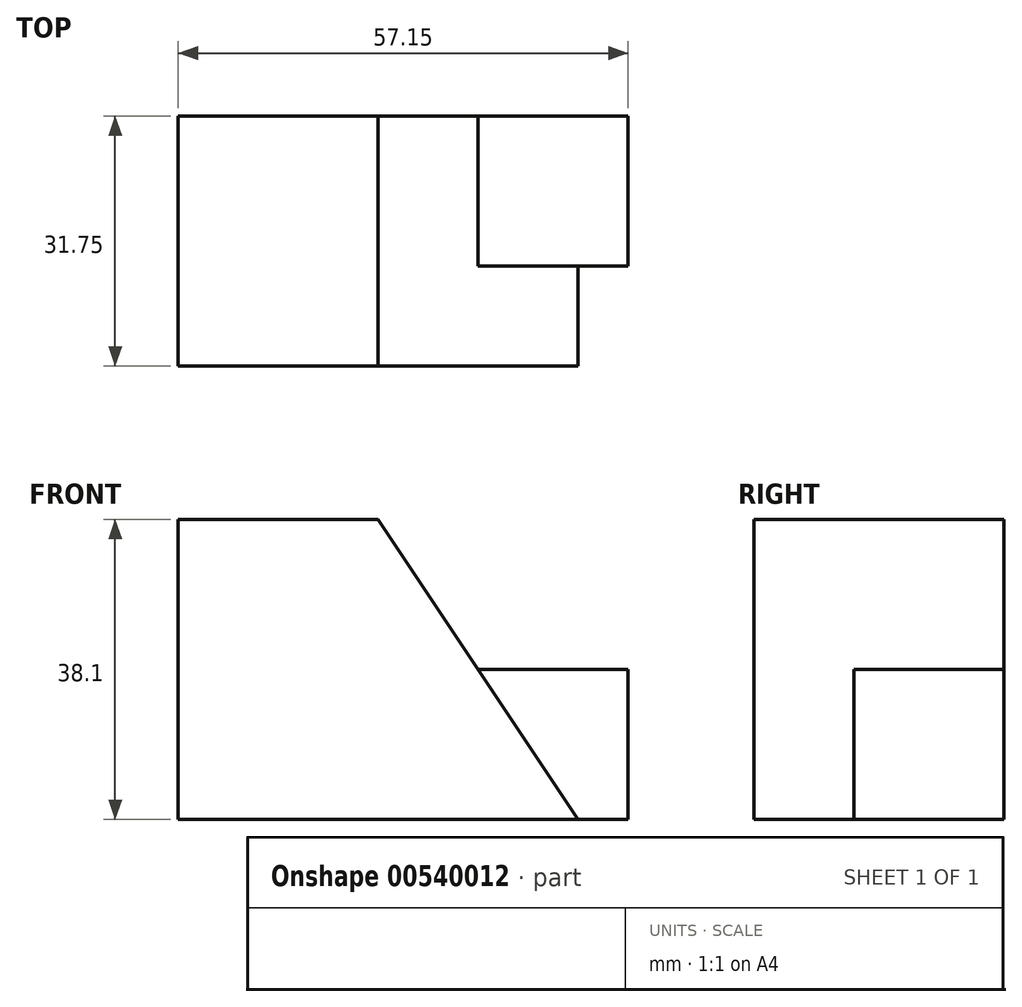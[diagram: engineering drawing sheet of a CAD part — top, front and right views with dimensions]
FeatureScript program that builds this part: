
annotation { "Feature Type Name" : "Feature", "Feature Type Description" : "" }
export const myFeature = defineFeature(function(context is Context, id is Id, definition is map)
    precondition{}
    {
        {
            var Q0;
            Q0=qCreatedBy(makeId("Front.planeOp"),FACE);
            var sketch = newSketch(context, id + "F0", { "sketchPlane" : qUnion([Q0])});
            skLineSegment(sketch, "E0", {"start": v(-71.12, 45.27) * mm, "end": v(-71.12, 7.17) * mm});
            skLineSegment(sketch, "E1", {"start": v(-71.12, 7.17) * mm, "end": v(-20.32, 7.17) * mm});
            skLineSegment(sketch, "E2", {"start": v(-20.32, 7.17) * mm, "end": v(-20.32, 45.27) * mm});
            skLineSegment(sketch, "E3", {"start": v(-71.12, 45.27) * mm, "end": v(-20.32, 45.27) * mm});
            skSolve(sketch);
        }
        {
            var Q0;
            Q0 = qSketchRegion(id + "F0", true);
            extrude(context, id + "F1", {"entities" : qUnion([Q0]), "depth" : 31.75 * mm, "offsetDistance" : 25.4 * mm});
        }
        {
            var Q0;
            Q0=makeQuery(id+"F1.opExtrude","CAP_FACE",FACE,{"disambiguationData":[OSD([sQuery(id+"F0.wireOp",EDGE,"E0"),sQuery(id+"F0.wireOp",EDGE,"E1"),sQuery(id+"F0.wireOp",EDGE,"E2"),sQuery(id+"F0.wireOp",EDGE,"E3")])],"isStart":false});
            var sketch = newSketch(context, id + "F2", { "sketchPlane" : qUnion([Q0])});
            skLineSegment(sketch, "E4", {"start": v(-20.32, 7.17) * mm, "end": v(-45.72, 45.27) * mm});
            skLineSegment(sketch, "E5", {"start": v(-45.72, 45.27) * mm, "end": v(-20.32, 45.27) * mm});
            skLineSegment(sketch, "E6", {"start": v(-20.32, 45.27) * mm, "end": v(-20.32, 7.17) * mm});
            skSolve(sketch);
        }
        {
            var Q0;
            Q0=makeQuery(id+"F2.imprint","IMPRINT",FACE,{"disambiguationData":[TD([[makeQuery(id+"F2.imprint","IMPRINT",EDGE,{"derivedFrom":sQuery(id+"F2.wireOp",EDGE,"E4")}),-1.0]])]});
            extrude(context, id + "F3", {"entities" : qUnion([Q0]), "operationType" : NewBodyOperationType.REMOVE, "oppositeDirection" : true, "depth" : 12.7 * mm, "offsetDistance" : 25.4 * mm});
        }
        {
            var Q0;
            Q0=makeQuery(id+"F3.boolean.opBoolean","COPY",FACE,{"derivedFrom":makeQuery(id+"F3.opExtrude","CAP_FACE",FACE,{"disambiguationData":[OSD([sQuery(id+"F2.wireOp",EDGE,"E4"),sQuery(id+"F2.wireOp",EDGE,"E5"),sQuery(id+"F2.wireOp",EDGE,"E6")])],"isStart":false})});
            var sketch = newSketch(context, id + "F4", { "sketchPlane" : qUnion([Q0])});
            skPoint(sketch, "E7.endSnap0", {"position": v(-33.02, 26.22) * mm});
            skLineSegment(sketch, "E8", {"start": v(-33.02, 26.22) * mm, "end": v(-20.32, 26.22) * mm});
            skLineSegment(sketch, "E9", {"start": v(-20.32, 26.22) * mm, "end": v(-20.32, 7.17) * mm});
            skSolve(sketch);
        }
        {
            var Q0;
            {var subQ0=sQuery(id+"F4.wireOp",EDGE,"E8");Q0=makeQuery(id+"F4.imprint","IMPRINT",FACE,{"disambiguationData":[TD([[makeQuery(id+"F4.imprint","IMPRINT",EDGE,{"derivedFrom":subQ0}),1.0]])]});}
            extrude(context, id + "F5", {"entities" : qUnion([Q0]), "operationType" : NewBodyOperationType.REMOVE, "oppositeDirection" : true, "depth" : 25.4 * mm, "offsetDistance" : 25.4 * mm});
        }
        {
            var Q0;
            Q0=makeQuery(id+"F1.opExtrude","SWEPT_FACE",FACE,{"disambiguationData":[OSD([sQuery(id+"F0.wireOp",EDGE,"E2")])]});
            extrude(context, id + "F6", {"entities" : qUnion([Q0]), "operationType" : NewBodyOperationType.ADD, "depth" : 6.35 * mm, "offsetDistance" : 25.4 * mm});
        }
    });
